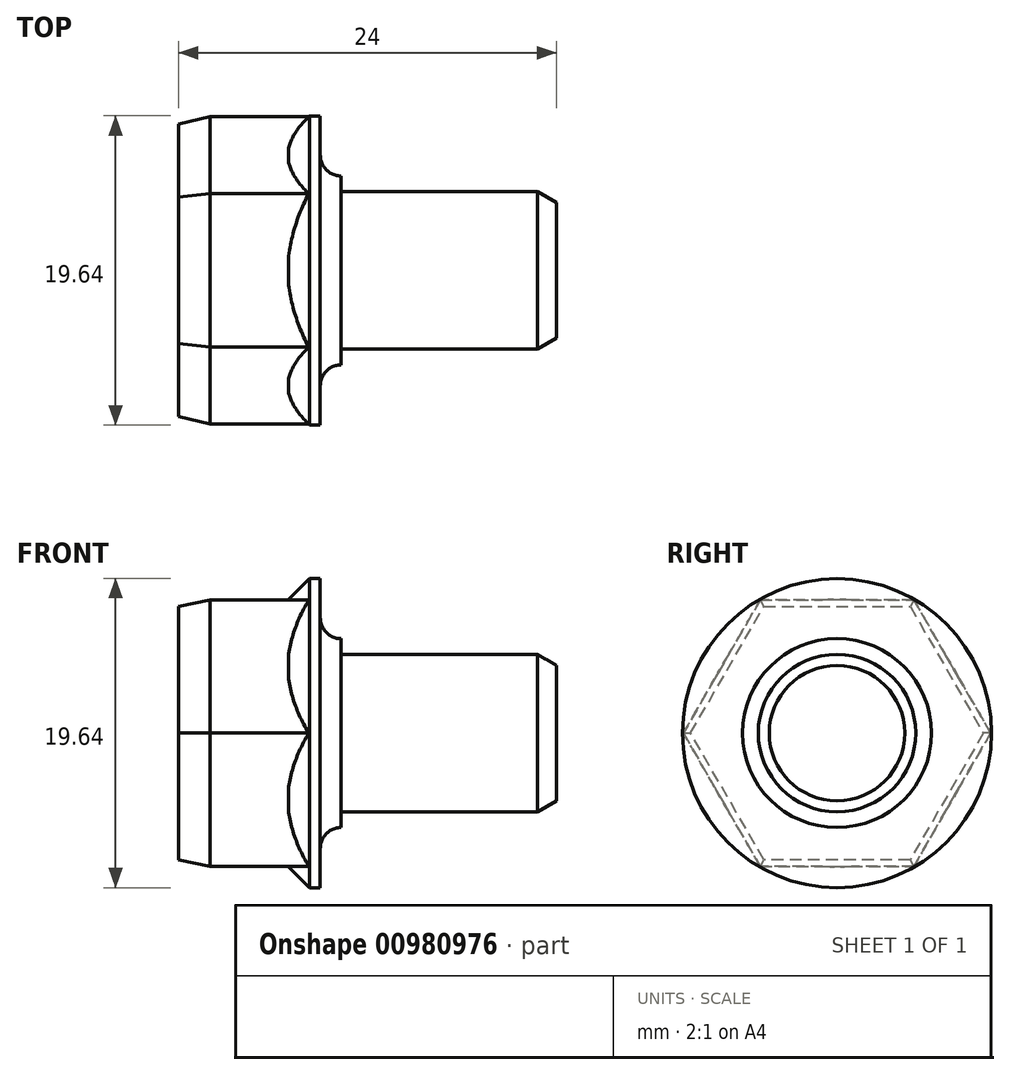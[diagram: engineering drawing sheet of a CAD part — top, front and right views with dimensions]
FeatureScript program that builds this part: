
annotation { "Feature Type Name" : "Feature", "Feature Type Description" : "" }
export const myFeature = defineFeature(function(context is Context, id is Id, definition is map)
    precondition{}
    {
        {
            var Q0;
            Q0=qCreatedBy(makeId("Right.planeOp"),FACE);
            var sketch = newSketch(context, id + "F0", { "sketchPlane" : qUnion([Q0])});
            skCircle(sketch, "E0.cCircle", {"center": v(0, 0) * mm, "radius": 8.45 * mm, "construction": true});
            skLineSegment(sketch, "E0.0", {"start": v(-4.88, 8.45) * mm, "end": v(4.88, 8.45) * mm});
            skLineSegment(sketch, "E0.1", {"start": v(4.88, 8.45) * mm, "end": v(9.76, 0) * mm});
            skLineSegment(sketch, "E0.2", {"start": v(9.76, 0) * mm, "end": v(4.88, -8.45) * mm});
            skLineSegment(sketch, "E0.3", {"start": v(4.88, -8.45) * mm, "end": v(-4.88, -8.45) * mm});
            skLineSegment(sketch, "E0.4", {"start": v(-4.88, -8.45) * mm, "end": v(-9.76, 0) * mm});
            skLineSegment(sketch, "E0.5", {"start": v(-9.76, 0) * mm, "end": v(-4.88, 8.45) * mm});
            skPoint(sketch, "E0.0.midPoint", {"position": v(0, 8.45) * mm});
            skSolve(sketch);
        }
        {
            var Q0;
            Q0=makeQuery(id+"F0.imprint","IMPRINT",FACE,{"disambiguationData":[TD([[makeQuery(id+"F0.imprint","IMPRINT",EDGE,{"derivedFrom":sQuery(id+"F0.wireOp",EDGE,"E0.0")}),-1.0]])]});
            extrude(context, id + "F1", {"entities" : qUnion([Q0]), "depth" : 9 * mm, "offsetDistance" : 25 * mm});
        }
        {
            var Q0;
            Q0=qCreatedBy(makeId("Front.planeOp"),FACE);
            var sketch = newSketch(context, id + "F2", { "sketchPlane" : qUnion([Q0])});
            skLineSegment(sketch, "E1", {"start": v(-6.63, 0) * mm, "end": v(40.7, 0) * mm, "construction": true});
            skLineSegment(sketch, "E2.bottom", {"start": v(7, 0) * mm, "end": v(9, 0) * mm});
            skLineSegment(sketch, "E2.top", {"start": v(7, 9.81) * mm, "end": v(9, 9.81) * mm});
            skLineSegment(sketch, "E2.left", {"start": v(7, 0) * mm, "end": v(7, 9.81) * mm});
            skLineSegment(sketch, "E2.right", {"start": v(9, 0) * mm, "end": v(9, 9.81) * mm});
            skLineSegment(sketch, "E3.bottom", {"start": v(9, 0) * mm, "end": v(24, 0) * mm});
            skLineSegment(sketch, "E3.top", {"start": v(10.31, 5) * mm, "end": v(24, 5) * mm});
            skLineSegment(sketch, "E3.right", {"start": v(24, 0) * mm, "end": v(24, 5) * mm});
            skLineSegment(sketch, "E4", {"start": v(8.31, 9.81) * mm, "end": v(7, 8.5) * mm});
            skArc(sketch, "E5", {"start": v(9, 7.32) * mm, "mid": v(9.39, 6.39) * mm, "end": v(10.31, 6) * mm});
            skLineSegment(sketch, "E6", {"start": v(10.31, 6) * mm, "end": v(10.31, 5) * mm});
            skLineSegment(sketch, "E7", {"start": v(11.47, 6) * mm, "end": v(14.9, 6) * mm, "construction": true});
            skSolve(sketch);
        }
        {
            var Q0;
            Q0=makeQuery(id+"F2.imprint","IMPRINT",FACE,{"disambiguationData":[TD([[makeQuery(id+"F2.imprint","IMPRINT",EDGE,{"derivedFrom":sQuery(id+"F2.wireOp",EDGE,"E2.right")}),-1.0]])]});
            var Q1;
            Q1=makeQuery(id+"F2.imprint","IMPRINT",FACE,{"disambiguationData":[TD([[makeQuery(id+"F2.imprint","IMPRINT",EDGE,{"derivedFrom":sQuery(id+"F2.wireOp",EDGE,"E3.bottom")}),1.0]])]});
            var Q2;
            Q2=makeQuery(id+"F2.imprint","IMPRINT",FACE,{"disambiguationData":[TD([[makeQuery(id+"F2.imprint","IMPRINT",EDGE,{"derivedFrom":sQuery(id+"F2.wireOp",EDGE,"E2.bottom")}),1.0]])]});
            var Q3;
            Q3=sQuery(id+"F2.wireOp",EDGE,"E1");
            revolve(context, id + "F3", {"operationType" : NewBodyOperationType.ADD, "surfaceOperationType" : NewSurfaceOperationType.NEW, "entities" : qUnion([Q0, Q1, Q2]), "axis" : qUnion([Q3]), "revolveType" : RevolveType.FULL});
        }
        {
            var Q0;
            Q0=makeQuery(id+"F1.opExtrude","CAP_FACE",FACE,{"disambiguationData":[OSD([sQuery(id+"F0.wireOp",EDGE,"E0.0"),sQuery(id+"F0.wireOp",EDGE,"E0.1"),sQuery(id+"F0.wireOp",EDGE,"E0.2"),sQuery(id+"F0.wireOp",EDGE,"E0.3"),sQuery(id+"F0.wireOp",EDGE,"E0.4"),sQuery(id+"F0.wireOp",EDGE,"E0.5")])],"isStart":true});
            chamfer(context, id + "F4", {"entities" : qUnion([Q0]), "chamferType" : ChamferType.TWO_OFFSETS, "width1" : 0.4 * mm, "oppositeDirection" : false, "width2" : 2 * mm, "tangentPropagation" : true});
        }
        {
            var Q0;
            Q0=makeQuery(id+"F3.opRevolve","SWEPT_EDGE",EDGE,{"disambiguationData":[OSD([sQuery(id+"F2.wireOp",EDGE,"E3.top"),sQuery(id+"F2.wireOp",EDGE,"E3.right")])]});
            chamfer(context, id + "F5", {"entities" : qUnion([Q0]), "chamferType" : ChamferType.TWO_OFFSETS, "width1" : 1.2 * mm, "oppositeDirection" : false, "width2" : 0.7 * mm, "tangentPropagation" : true});
        }
    });
